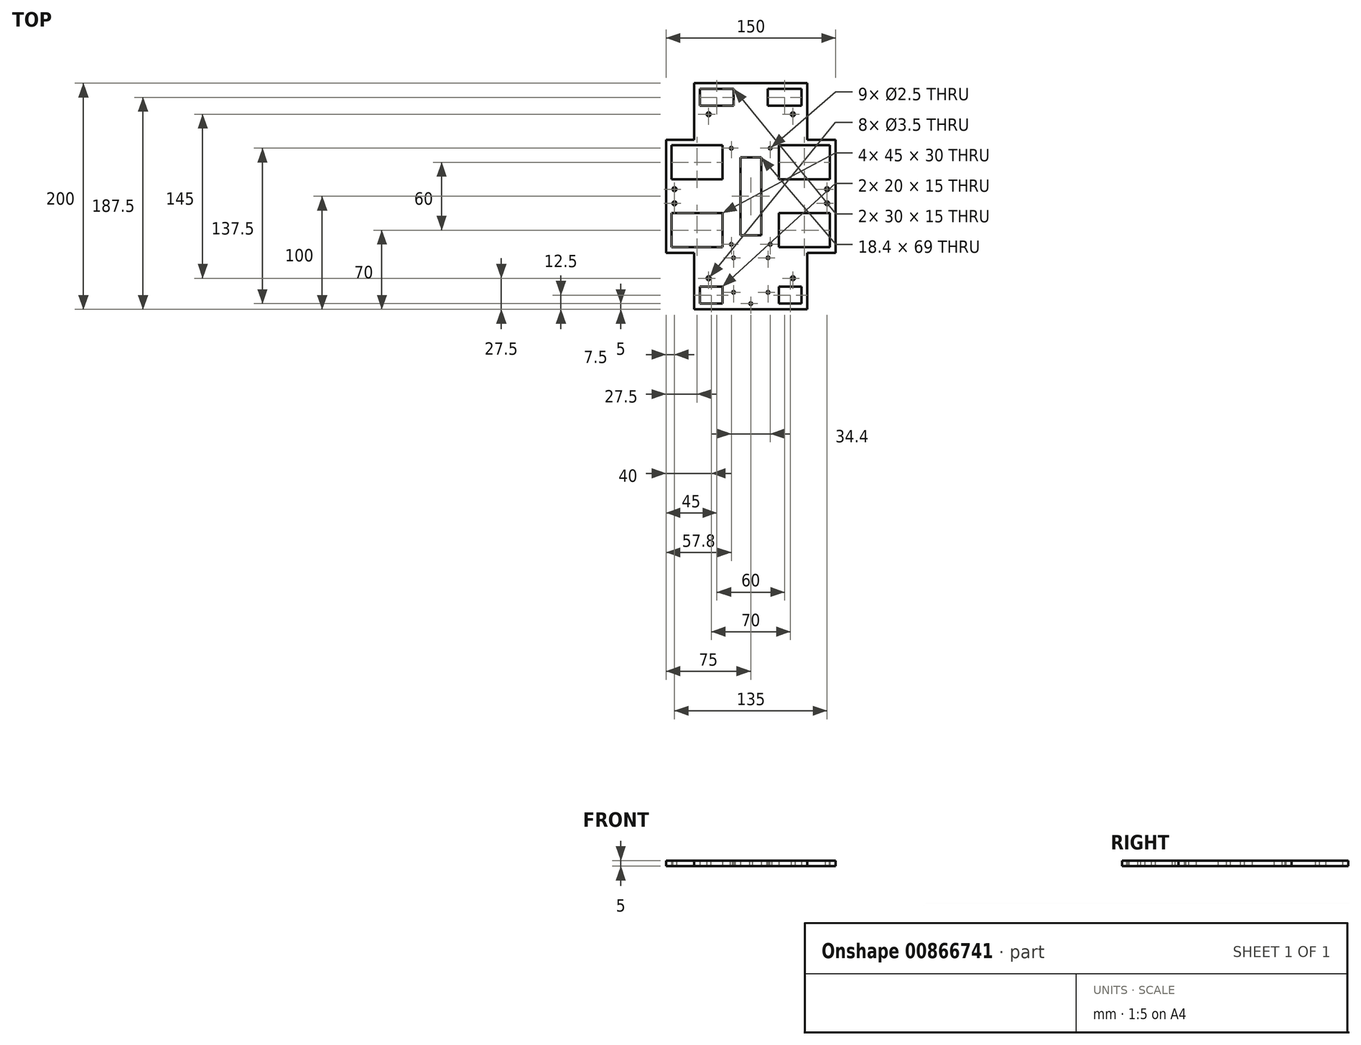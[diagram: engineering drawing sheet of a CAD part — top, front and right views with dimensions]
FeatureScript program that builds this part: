
annotation { "Feature Type Name" : "Feature", "Feature Type Description" : "" }
export const myFeature = defineFeature(function(context is Context, id is Id, definition is map)
    precondition{}
    {
        {
            assignVariable(context, id + "F0", {"variableType" : VariableType.LENGTH, "name" : "RackThickness", "lengthValue" : 5 * mm});
        }
        {
            var Q0;
            Q0=qCreatedBy(makeId("Top.planeOp"),FACE);
            var sketch = newSketch(context, id + "F1", { "sketchPlane" : qUnion([Q0])});
            skLineSegment(sketch, "E0.bottom", {"start": v(-50, 100) * mm, "end": v(50, 100) * mm});
            skLineSegment(sketch, "E0.top", {"start": v(-50, -100) * mm, "end": v(50, -100) * mm});
            skLineSegment(sketch, "E0.left", {"start": v(-50, 100) * mm, "end": v(-50, -100) * mm});
            skLineSegment(sketch, "E0.right", {"start": v(50, 100) * mm, "end": v(50, -100) * mm});
            skPoint(sketch, "E0.middle", {"position": v(0, 0) * mm});
            skLineSegment(sketch, "E1.bottom", {"start": v(75, -50) * mm, "end": v(-75, -50) * mm});
            skLineSegment(sketch, "E1.top", {"start": v(75, 50) * mm, "end": v(-75, 50) * mm});
            skLineSegment(sketch, "E1.left", {"start": v(75, -50) * mm, "end": v(75, 50) * mm});
            skLineSegment(sketch, "E1.right", {"start": v(-75, -50) * mm, "end": v(-75, 50) * mm});
            skLineSegment(sketch, "E2.bottom", {"start": v(37.25, -72.5) * mm, "end": v(-37.25, -72.5) * mm});
            skLineSegment(sketch, "E2.top", {"start": v(37.25, 72.5) * mm, "end": v(-37.25, 72.5) * mm});
            skLineSegment(sketch, "E2.left", {"start": v(37.25, -72.5) * mm, "end": v(37.25, 72.5) * mm});
            skLineSegment(sketch, "E2.right", {"start": v(-37.25, -72.5) * mm, "end": v(-37.25, 72.5) * mm});
            skLineSegment(sketch, "E3.bottom", {"start": v(67.5, -6.25) * mm, "end": v(-67.5, -6.25) * mm});
            skLineSegment(sketch, "E3.top", {"start": v(67.5, 6.25) * mm, "end": v(-67.5, 6.25) * mm});
            skLineSegment(sketch, "E3.left", {"start": v(67.5, -6.25) * mm, "end": v(67.5, 6.25) * mm});
            skLineSegment(sketch, "E3.right", {"start": v(-67.5, -6.25) * mm, "end": v(-67.5, 6.25) * mm});
            skCircle(sketch, "E4", {"center": v(-37.25, 72.5) * mm, "radius": 1.75 * mm});
            skCircle(sketch, "E5", {"center": v(37.25, 72.5) * mm, "radius": 1.75 * mm});
            skCircle(sketch, "E6", {"center": v(-67.5, 6.25) * mm, "radius": 1.75 * mm});
            skCircle(sketch, "E7", {"center": v(67.5, 6.25) * mm, "radius": 1.75 * mm});
            skCircle(sketch, "E8", {"center": v(67.5, -6.25) * mm, "radius": 1.75 * mm});
            skCircle(sketch, "E9", {"center": v(-67.5, -6.25) * mm, "radius": 1.75 * mm});
            skCircle(sketch, "E10", {"center": v(-37.25, -72.5) * mm, "radius": 1.75 * mm});
            skCircle(sketch, "E11", {"center": v(37.25, -72.5) * mm, "radius": 1.75 * mm});
            skPoint(sketch, "E12", {"position": v(-70, 50) * mm});
            skPoint(sketch, "E13", {"position": v(-75, 45) * mm});
            skPoint(sketch, "E14", {"position": v(-75, -45) * mm});
            skPoint(sketch, "E15", {"position": v(-70, -50) * mm});
            skPoint(sketch, "E16", {"position": v(-50, -95) * mm});
            skPoint(sketch, "E17", {"position": v(-45, -100) * mm});
            skPoint(sketch, "E18", {"position": v(-50, 95) * mm});
            skPoint(sketch, "E19", {"position": v(-45, 100) * mm});
            skPoint(sketch, "E20", {"position": v(45, -100) * mm});
            skPoint(sketch, "E21", {"position": v(50, -95) * mm});
            skPoint(sketch, "E22", {"position": v(70, -50) * mm});
            skPoint(sketch, "E23", {"position": v(75, -45) * mm});
            skPoint(sketch, "E24", {"position": v(75, 45) * mm});
            skPoint(sketch, "E25", {"position": v(70, 50) * mm});
            skPoint(sketch, "E26", {"position": v(50, 95) * mm});
            skPoint(sketch, "E27", {"position": v(45, 100) * mm});
            skLineSegment(sketch, "E28.bottom", {"start": v(-45, 95) * mm, "end": v(-15, 95) * mm});
            skLineSegment(sketch, "E28.top", {"start": v(-45, 80) * mm, "end": v(-15, 80) * mm});
            skLineSegment(sketch, "E28.left", {"start": v(-45, 95) * mm, "end": v(-45, 80) * mm});
            skLineSegment(sketch, "E28.right", {"start": v(-15, 95) * mm, "end": v(-15, 80) * mm});
            skLineSegment(sketch, "E29.bottom", {"start": v(45, 95) * mm, "end": v(15, 95) * mm});
            skLineSegment(sketch, "E29.top", {"start": v(45, 80) * mm, "end": v(15, 80) * mm});
            skLineSegment(sketch, "E29.left", {"start": v(45, 95) * mm, "end": v(45, 80) * mm});
            skLineSegment(sketch, "E29.right", {"start": v(15, 95) * mm, "end": v(15, 80) * mm});
            skLineSegment(sketch, "E30.bottom", {"start": v(70, 45) * mm, "end": v(25, 45) * mm});
            skLineSegment(sketch, "E30.top", {"start": v(70, 15) * mm, "end": v(25, 15) * mm});
            skLineSegment(sketch, "E30.left", {"start": v(70, 45) * mm, "end": v(70, 15) * mm});
            skLineSegment(sketch, "E30.right", {"start": v(25, 45) * mm, "end": v(25, 15) * mm});
            skLineSegment(sketch, "E31.bottom", {"start": v(70, -45) * mm, "end": v(25, -45) * mm});
            skLineSegment(sketch, "E31.top", {"start": v(70, -15) * mm, "end": v(25, -15) * mm});
            skLineSegment(sketch, "E31.left", {"start": v(70, -45) * mm, "end": v(70, -15) * mm});
            skLineSegment(sketch, "E31.right", {"start": v(25, -45) * mm, "end": v(25, -15) * mm});
            skLineSegment(sketch, "E32.bottom", {"start": v(-70, 45) * mm, "end": v(-25, 45) * mm});
            skLineSegment(sketch, "E32.top", {"start": v(-70, 15) * mm, "end": v(-25, 15) * mm});
            skLineSegment(sketch, "E32.left", {"start": v(-70, 45) * mm, "end": v(-70, 15) * mm});
            skLineSegment(sketch, "E32.right", {"start": v(-25, 45) * mm, "end": v(-25, 15) * mm});
            skLineSegment(sketch, "E33.bottom", {"start": v(-70, -45) * mm, "end": v(-25, -45) * mm});
            skLineSegment(sketch, "E33.top", {"start": v(-70, -15) * mm, "end": v(-25, -15) * mm});
            skLineSegment(sketch, "E33.left", {"start": v(-70, -45) * mm, "end": v(-70, -15) * mm});
            skLineSegment(sketch, "E33.right", {"start": v(-25, -45) * mm, "end": v(-25, -15) * mm});
            skLineSegment(sketch, "E34.bottom", {"start": v(-45, -95) * mm, "end": v(-25, -95) * mm});
            skLineSegment(sketch, "E34.top", {"start": v(-45, -80) * mm, "end": v(-25, -80) * mm});
            skLineSegment(sketch, "E34.left", {"start": v(-45, -95) * mm, "end": v(-45, -80) * mm});
            skLineSegment(sketch, "E34.right", {"start": v(-25, -95) * mm, "end": v(-25, -80) * mm});
            skLineSegment(sketch, "E35.bottom", {"start": v(45, -95) * mm, "end": v(25, -95) * mm});
            skLineSegment(sketch, "E35.top", {"start": v(45, -80) * mm, "end": v(25, -80) * mm});
            skLineSegment(sketch, "E35.left", {"start": v(45, -95) * mm, "end": v(45, -80) * mm});
            skLineSegment(sketch, "E35.right", {"start": v(25, -95) * mm, "end": v(25, -80) * mm});
            skSolve(sketch);
        }
        {
            var Q0;
            {var subQ0=sQuery(id+"F1.wireOp",EDGE,"E1.top");var subQ1=sQuery(id+"F1.wireOp",EDGE,"E0.left");var subQ2=makeQuery(id+"F1.imprint","INTERSECT",VERTEX,{"derivedFrom":[subQ1,subQ0]});Q0=makeQuery(id+"F1.imprint","IMPRINT",FACE,{"disambiguationData":[TD([[makeQuery(id+"F1.imprint","IMPRINT",EDGE,{"disambiguationData":[TD([[subQ2,-1.0]])],"derivedFrom":subQ1}),1.0]])]});}
            var sketch = newSketch(context, id + "F2", { "sketchPlane" : qUnion([Q0])});
            skLineSegment(sketch, "E36.bottom", {"start": v(17.2, -42.5) * mm, "end": v(-17.2, -42.5) * mm});
            skLineSegment(sketch, "E36.top", {"start": v(17.2, 42.5) * mm, "end": v(-17.2, 42.5) * mm});
            skLineSegment(sketch, "E36.left", {"start": v(17.2, -42.5) * mm, "end": v(17.2, 42.5) * mm});
            skLineSegment(sketch, "E36.right", {"start": v(-17.2, -42.5) * mm, "end": v(-17.2, 42.5) * mm});
            skPoint(sketch, "E36.middle", {"position": v(0, 0) * mm});
            skCircle(sketch, "E37", {"center": v(-17.2, 42.5) * mm, "radius": 1.25 * mm});
            skCircle(sketch, "E38", {"center": v(17.2, 42.5) * mm, "radius": 1.25 * mm});
            skCircle(sketch, "E39", {"center": v(-17.2, -42.5) * mm, "radius": 1.25 * mm});
            skCircle(sketch, "E40", {"center": v(17.2, -42.5) * mm, "radius": 1.25 * mm});
            skPoint(sketch, "E41", {"position": v(0, -100) * mm});
            skLineSegment(sketch, "E42", {"start": v(0, -100) * mm, "end": v(0, -69.75) * mm});
            skLineSegment(sketch, "E43.bottom", {"start": v(15.25, -54.5) * mm, "end": v(-15.25, -54.5) * mm});
            skLineSegment(sketch, "E43.top", {"start": v(15.25, -85) * mm, "end": v(-15.25, -85) * mm});
            skLineSegment(sketch, "E43.left", {"start": v(15.25, -54.5) * mm, "end": v(15.25, -85) * mm});
            skLineSegment(sketch, "E43.right", {"start": v(-15.25, -54.5) * mm, "end": v(-15.25, -85) * mm});
            skPoint(sketch, "E43.middle", {"position": v(0, -69.75) * mm});
            skCircle(sketch, "E44", {"center": v(-15.25, -54.5) * mm, "radius": 1.25 * mm});
            skCircle(sketch, "E45", {"center": v(15.25, -54.5) * mm, "radius": 1.25 * mm});
            skCircle(sketch, "E46", {"center": v(15.25, -85) * mm, "radius": 1.25 * mm});
            skCircle(sketch, "E47", {"center": v(-15.25, -85) * mm, "radius": 1.25 * mm});
            skLineSegment(sketch, "E48.bottom", {"start": v(9.2, 34.5) * mm, "end": v(-9.2, 34.5) * mm});
            skLineSegment(sketch, "E48.top", {"start": v(9.2, -34.5) * mm, "end": v(-9.2, -34.5) * mm});
            skLineSegment(sketch, "E48.left", {"start": v(9.2, 34.5) * mm, "end": v(9.2, -34.5) * mm});
            skLineSegment(sketch, "E48.right", {"start": v(-9.2, 34.5) * mm, "end": v(-9.2, -34.5) * mm});
            skPoint(sketch, "E49", {"position": v(0, -95) * mm});
            skPoint(sketch, "E50", {"position": v(0, -85) * mm});
            skCircle(sketch, "E51", {"center": v(0, -85) * mm, "radius": 1.25 * mm});
            skCircle(sketch, "E52", {"center": v(0, -95) * mm, "radius": 1.25 * mm});
            skSolve(sketch);
        }
        {
            var Q0;
            Q0 = qSketchRegion(id + "F1", true);
            var Q1;
            {var subQ1=sQuery(id+"F1.wireOp",EDGE,"E1.bottom");var subQ5=sQuery(id+"F1.wireOp",EDGE,"E2.left");var subQ6=makeQuery(id+"F1.imprint","INTERSECT",VERTEX,{"derivedFrom":[subQ1,subQ5]});Q1=makeQuery(id+"F1.imprint","IMPRINT",FACE,{"disambiguationData":[TD([[makeQuery(id+"F1.imprint","IMPRINT",EDGE,{"disambiguationData":[TD([[subQ6,-1.0]])],"derivedFrom":subQ1}),1.0]])]});}
            var Q2;
            {var subQ0=sQuery(id+"F1.wireOp",EDGE,"E31.right");Q2=makeQuery(id+"F1.imprint","IMPRINT",FACE,{"disambiguationData":[TD([[makeQuery(id+"F1.imprint","IMPRINT",EDGE,{"derivedFrom":subQ0}),1.0]])]});}
            var Q3;
            {var subQ4=sQuery(id+"F1.wireOp",EDGE,"E30.right");Q3=makeQuery(id+"F1.imprint","IMPRINT",FACE,{"disambiguationData":[TD([[makeQuery(id+"F1.imprint","IMPRINT",EDGE,{"derivedFrom":subQ4}),-1.0]])]});}
            var Q4;
            {var subQ1=sQuery(id+"F1.wireOp",EDGE,"E1.top");var subQ9=sQuery(id+"F1.wireOp",EDGE,"E2.left");var subQ10=makeQuery(id+"F1.imprint","INTERSECT",VERTEX,{"derivedFrom":[subQ1,subQ9]});Q4=makeQuery(id+"F1.imprint","IMPRINT",FACE,{"disambiguationData":[TD([[makeQuery(id+"F1.imprint","IMPRINT",EDGE,{"disambiguationData":[TD([[subQ10,-1.0]])],"derivedFrom":subQ1}),-1.0]])]});}
            var Q5;
            {var subQ0=sQuery(id+"F1.wireOp",EDGE,"E3.bottom");var subQ1=sQuery(id+"F1.wireOp",EDGE,"E2.left");var subQ2=makeQuery(id+"F1.imprint","INTERSECT",VERTEX,{"derivedFrom":[subQ1,subQ0]});Q5=makeQuery(id+"F1.imprint","IMPRINT",FACE,{"disambiguationData":[TD([[makeQuery(id+"F1.imprint","IMPRINT",EDGE,{"disambiguationData":[TD([[subQ2,-1.0]])],"derivedFrom":subQ1}),1.0]])]});}
            var Q6;
            {var subQ0=sQuery(id+"F1.wireOp",EDGE,"E32.top");var subQ1=sQuery(id+"F1.wireOp",EDGE,"E0.left");var subQ2=makeQuery(id+"F1.imprint","INTERSECT",VERTEX,{"derivedFrom":[subQ1,subQ0]});Q6=makeQuery(id+"F1.imprint","IMPRINT",FACE,{"disambiguationData":[TD([[makeQuery(id+"F1.imprint","IMPRINT",EDGE,{"disambiguationData":[TD([[subQ2,-1.0]])],"derivedFrom":subQ1}),1.0]])]});}
            var Q7;
            {var subQ0=sQuery(id+"F1.wireOp",EDGE,"E3.bottom");var subQ1=sQuery(id+"F1.wireOp",EDGE,"E0.left");var subQ2=makeQuery(id+"F1.imprint","INTERSECT",VERTEX,{"derivedFrom":[subQ1,subQ0]});Q7=makeQuery(id+"F1.imprint","IMPRINT",FACE,{"disambiguationData":[TD([[makeQuery(id+"F1.imprint","IMPRINT",EDGE,{"disambiguationData":[TD([[subQ2,-1.0]])],"derivedFrom":subQ1}),1.0]])]});}
            var Q8;
            {var subQ0=sQuery(id+"F1.wireOp",EDGE,"E3.top");var subQ1=sQuery(id+"F1.wireOp",EDGE,"E0.left");var subQ2=makeQuery(id+"F1.imprint","INTERSECT",VERTEX,{"derivedFrom":[subQ1,subQ0]});Q8=makeQuery(id+"F1.imprint","IMPRINT",FACE,{"disambiguationData":[TD([[makeQuery(id+"F1.imprint","IMPRINT",EDGE,{"disambiguationData":[TD([[subQ2,-1.0]])],"derivedFrom":subQ1}),1.0]])]});}
            var Q9;
            {var subQ0=sQuery(id+"F1.wireOp",EDGE,"E3.bottom");var subQ1=sQuery(id+"F1.wireOp",EDGE,"E0.right");var subQ2=makeQuery(id+"F1.imprint","INTERSECT",VERTEX,{"derivedFrom":[subQ1,subQ0]});Q9=makeQuery(id+"F1.imprint","IMPRINT",FACE,{"disambiguationData":[TD([[makeQuery(id+"F1.imprint","IMPRINT",EDGE,{"disambiguationData":[TD([[subQ2,-1.0]])],"derivedFrom":subQ1}),-1.0]])]});}
            var Q10;
            {var subQ0=sQuery(id+"F1.wireOp",EDGE,"E3.top");var subQ1=sQuery(id+"F1.wireOp",EDGE,"E0.right");var subQ2=makeQuery(id+"F1.imprint","INTERSECT",VERTEX,{"derivedFrom":[subQ1,subQ0]});Q10=makeQuery(id+"F1.imprint","IMPRINT",FACE,{"disambiguationData":[TD([[makeQuery(id+"F1.imprint","IMPRINT",EDGE,{"disambiguationData":[TD([[subQ2,-1.0]])],"derivedFrom":subQ1}),-1.0]])]});}
            var Q11;
            {var subQ0=sQuery(id+"F1.wireOp",EDGE,"E30.top");var subQ1=sQuery(id+"F1.wireOp",EDGE,"E0.right");var subQ2=makeQuery(id+"F1.imprint","INTERSECT",VERTEX,{"derivedFrom":[subQ1,subQ0]});Q11=makeQuery(id+"F1.imprint","IMPRINT",FACE,{"disambiguationData":[TD([[makeQuery(id+"F1.imprint","IMPRINT",EDGE,{"disambiguationData":[TD([[subQ2,-1.0]])],"derivedFrom":subQ1}),-1.0]])]});}
            var Q12;
            {var subQ0=sQuery(id+"F1.wireOp",EDGE,"E3.top");var subQ1=sQuery(id+"F1.wireOp",EDGE,"E0.right");var subQ2=makeQuery(id+"F1.imprint","INTERSECT",VERTEX,{"derivedFrom":[subQ1,subQ0]});Q12=makeQuery(id+"F1.imprint","IMPRINT",FACE,{"disambiguationData":[TD([[makeQuery(id+"F1.imprint","IMPRINT",EDGE,{"disambiguationData":[TD([[subQ2,-1.0]])],"derivedFrom":subQ1}),1.0]])]});}
            var Q13;
            {var subQ5=sQuery(id+"F1.wireOp",EDGE,"E3.top");var subQ6=sQuery(id+"F1.wireOp",EDGE,"E0.left");var subQ7=makeQuery(id+"F1.imprint","INTERSECT",VERTEX,{"derivedFrom":[subQ6,subQ5]});Q13=makeQuery(id+"F1.imprint","IMPRINT",FACE,{"disambiguationData":[TD([[makeQuery(id+"F1.imprint","IMPRINT",EDGE,{"disambiguationData":[TD([[subQ7,-1.0]])],"derivedFrom":subQ6}),-1.0]])]});}
            extrude(context, id + "F3", {"entities" : qUnion([Q0, Q1, Q2, Q3, Q4, Q5, Q6, Q7, Q8, Q9, Q10, Q11, Q12, Q13]), "depth" : getVariable(context, 'RackThickness'), "offsetDistance" : 25 * mm});
        }
        {
            var Q0;
            {var subQ0=sQuery(id+"F2.wireOp",EDGE,"E43.left");var subQ1=sQuery(id+"F2.wireOp",EDGE,"E43.top");var subQ2=makeQuery(id+"F2.imprint","INTERSECT",VERTEX,{"derivedFrom":[subQ1,subQ0]});Q0=makeQuery(id+"F2.imprint","IMPRINT",FACE,{"disambiguationData":[TD([[makeQuery(id+"F2.imprint","IMPRINT",EDGE,{"disambiguationData":[TD([[subQ2,-1.0]])],"derivedFrom":subQ1}),1.0]])]});}
            var Q1;
            {var subQ0=sQuery(id+"F2.wireOp",EDGE,"E51");var subQ1=sQuery(id+"F2.wireOp",EDGE,"E42");var subQ2=makeQuery(id+"F2.imprint","INTERSECT",VERTEX,{"disambiguationData":[OD(0.0)],"derivedFrom":[subQ1,subQ0]});Q1=makeQuery(id+"F2.imprint","IMPRINT",FACE,{"disambiguationData":[TD([[makeQuery(id+"F2.imprint","IMPRINT",EDGE,{"disambiguationData":[TD([[subQ2,-1.0]])],"derivedFrom":subQ1}),1.0]])]});}
            var Q2;
            {var subQ0=sQuery(id+"F2.wireOp",EDGE,"E51");var subQ1=sQuery(id+"F2.wireOp",EDGE,"E42");var subQ2=makeQuery(id+"F2.imprint","INTERSECT",VERTEX,{"disambiguationData":[OD(1.0)],"derivedFrom":[subQ1,subQ0]});Q2=makeQuery(id+"F2.imprint","IMPRINT",FACE,{"disambiguationData":[TD([[makeQuery(id+"F2.imprint","IMPRINT",EDGE,{"disambiguationData":[TD([[subQ2,1.0]])],"derivedFrom":subQ1}),-1.0]])]});}
            var Q3;
            {var subQ0=sQuery(id+"F2.wireOp",EDGE,"E51");var subQ1=sQuery(id+"F2.wireOp",EDGE,"E42");var subQ2=makeQuery(id+"F2.imprint","INTERSECT",VERTEX,{"disambiguationData":[OD(0.0)],"derivedFrom":[subQ1,subQ0]});Q3=makeQuery(id+"F2.imprint","IMPRINT",FACE,{"disambiguationData":[TD([[makeQuery(id+"F2.imprint","IMPRINT",EDGE,{"disambiguationData":[TD([[subQ2,-1.0]])],"derivedFrom":subQ1}),-1.0]])]});}
            var Q4;
            {var subQ0=sQuery(id+"F2.wireOp",EDGE,"E51");var subQ1=sQuery(id+"F2.wireOp",EDGE,"E42");var subQ2=makeQuery(id+"F2.imprint","INTERSECT",VERTEX,{"disambiguationData":[OD(1.0)],"derivedFrom":[subQ1,subQ0]});Q4=makeQuery(id+"F2.imprint","IMPRINT",FACE,{"disambiguationData":[TD([[makeQuery(id+"F2.imprint","IMPRINT",EDGE,{"disambiguationData":[TD([[subQ2,1.0]])],"derivedFrom":subQ1}),1.0]])]});}
            var Q5;
            {var subQ0=sQuery(id+"F2.wireOp",EDGE,"E52");var subQ1=sQuery(id+"F2.wireOp",EDGE,"E42");var subQ2=makeQuery(id+"F2.imprint","INTERSECT",VERTEX,{"disambiguationData":[OD(0.0)],"derivedFrom":[subQ1,subQ0]});Q5=makeQuery(id+"F2.imprint","IMPRINT",FACE,{"disambiguationData":[TD([[makeQuery(id+"F2.imprint","IMPRINT",EDGE,{"disambiguationData":[TD([[subQ2,-1.0]])],"derivedFrom":subQ1}),1.0]])]});}
            var Q6;
            {var subQ0=sQuery(id+"F2.wireOp",EDGE,"E52");var subQ1=sQuery(id+"F2.wireOp",EDGE,"E42");var subQ2=makeQuery(id+"F2.imprint","INTERSECT",VERTEX,{"disambiguationData":[OD(0.0)],"derivedFrom":[subQ1,subQ0]});Q6=makeQuery(id+"F2.imprint","IMPRINT",FACE,{"disambiguationData":[TD([[makeQuery(id+"F2.imprint","IMPRINT",EDGE,{"disambiguationData":[TD([[subQ2,-1.0]])],"derivedFrom":subQ1}),-1.0]])]});}
            var Q7;
            {var subQ0=sQuery(id+"F2.wireOp",EDGE,"E43.left");var subQ1=sQuery(id+"F2.wireOp",EDGE,"E43.top");var subQ2=makeQuery(id+"F2.imprint","INTERSECT",VERTEX,{"derivedFrom":[subQ1,subQ0]});Q7=makeQuery(id+"F2.imprint","IMPRINT",FACE,{"disambiguationData":[TD([[makeQuery(id+"F2.imprint","IMPRINT",EDGE,{"disambiguationData":[TD([[subQ2,-1.0]])],"derivedFrom":subQ1}),-1.0]])]});}
            var Q8;
            {var subQ0=sQuery(id+"F2.wireOp",EDGE,"E43.right");var subQ1=sQuery(id+"F2.wireOp",EDGE,"E43.top");var subQ2=makeQuery(id+"F2.imprint","INTERSECT",VERTEX,{"derivedFrom":[subQ1,subQ0]});Q8=makeQuery(id+"F2.imprint","IMPRINT",FACE,{"disambiguationData":[TD([[makeQuery(id+"F2.imprint","IMPRINT",EDGE,{"disambiguationData":[TD([[subQ2,1.0]])],"derivedFrom":subQ1}),1.0]])]});}
            var Q9;
            {var subQ0=sQuery(id+"F2.wireOp",EDGE,"E43.right");var subQ1=sQuery(id+"F2.wireOp",EDGE,"E43.top");var subQ2=makeQuery(id+"F2.imprint","INTERSECT",VERTEX,{"derivedFrom":[subQ1,subQ0]});Q9=makeQuery(id+"F2.imprint","IMPRINT",FACE,{"disambiguationData":[TD([[makeQuery(id+"F2.imprint","IMPRINT",EDGE,{"disambiguationData":[TD([[subQ2,1.0]])],"derivedFrom":subQ1}),-1.0]])]});}
            var Q10;
            {var subQ0=sQuery(id+"F2.wireOp",EDGE,"E43.left");var subQ1=sQuery(id+"F2.wireOp",EDGE,"E43.bottom");var subQ2=makeQuery(id+"F2.imprint","INTERSECT",VERTEX,{"derivedFrom":[subQ1,subQ0]});Q10=makeQuery(id+"F2.imprint","IMPRINT",FACE,{"disambiguationData":[TD([[makeQuery(id+"F2.imprint","IMPRINT",EDGE,{"disambiguationData":[TD([[subQ2,-1.0]])],"derivedFrom":subQ1}),-1.0]])]});}
            var Q11;
            {var subQ0=sQuery(id+"F2.wireOp",EDGE,"E43.left");var subQ1=sQuery(id+"F2.wireOp",EDGE,"E43.bottom");var subQ2=makeQuery(id+"F2.imprint","INTERSECT",VERTEX,{"derivedFrom":[subQ1,subQ0]});Q11=makeQuery(id+"F2.imprint","IMPRINT",FACE,{"disambiguationData":[TD([[makeQuery(id+"F2.imprint","IMPRINT",EDGE,{"disambiguationData":[TD([[subQ2,-1.0]])],"derivedFrom":subQ1}),1.0]])]});}
            var Q12;
            {var subQ0=sQuery(id+"F2.wireOp",EDGE,"E43.right");var subQ1=sQuery(id+"F2.wireOp",EDGE,"E43.bottom");var subQ2=makeQuery(id+"F2.imprint","INTERSECT",VERTEX,{"derivedFrom":[subQ1,subQ0]});Q12=makeQuery(id+"F2.imprint","IMPRINT",FACE,{"disambiguationData":[TD([[makeQuery(id+"F2.imprint","IMPRINT",EDGE,{"disambiguationData":[TD([[subQ2,1.0]])],"derivedFrom":subQ1}),1.0]])]});}
            var Q13;
            {var subQ0=sQuery(id+"F2.wireOp",EDGE,"E43.right");var subQ1=sQuery(id+"F2.wireOp",EDGE,"E43.bottom");var subQ2=makeQuery(id+"F2.imprint","INTERSECT",VERTEX,{"derivedFrom":[subQ1,subQ0]});Q13=makeQuery(id+"F2.imprint","IMPRINT",FACE,{"disambiguationData":[TD([[makeQuery(id+"F2.imprint","IMPRINT",EDGE,{"disambiguationData":[TD([[subQ2,1.0]])],"derivedFrom":subQ1}),-1.0]])]});}
            var Q14;
            {var subQ0=sQuery(id+"F2.wireOp",EDGE,"E36.left");var subQ1=sQuery(id+"F2.wireOp",EDGE,"E36.bottom");var subQ2=makeQuery(id+"F2.imprint","INTERSECT",VERTEX,{"derivedFrom":[subQ1,subQ0]});Q14=makeQuery(id+"F2.imprint","IMPRINT",FACE,{"disambiguationData":[TD([[makeQuery(id+"F2.imprint","IMPRINT",EDGE,{"disambiguationData":[TD([[subQ2,-1.0]])],"derivedFrom":subQ1}),1.0]])]});}
            var Q15;
            {var subQ0=sQuery(id+"F2.wireOp",EDGE,"E36.left");var subQ1=sQuery(id+"F2.wireOp",EDGE,"E36.bottom");var subQ2=makeQuery(id+"F2.imprint","INTERSECT",VERTEX,{"derivedFrom":[subQ1,subQ0]});Q15=makeQuery(id+"F2.imprint","IMPRINT",FACE,{"disambiguationData":[TD([[makeQuery(id+"F2.imprint","IMPRINT",EDGE,{"disambiguationData":[TD([[subQ2,-1.0]])],"derivedFrom":subQ1}),-1.0]])]});}
            var Q16;
            {var subQ0=sQuery(id+"F2.wireOp",EDGE,"E36.right");var subQ1=sQuery(id+"F2.wireOp",EDGE,"E36.bottom");var subQ2=makeQuery(id+"F2.imprint","INTERSECT",VERTEX,{"derivedFrom":[subQ1,subQ0]});Q16=makeQuery(id+"F2.imprint","IMPRINT",FACE,{"disambiguationData":[TD([[makeQuery(id+"F2.imprint","IMPRINT",EDGE,{"disambiguationData":[TD([[subQ2,1.0]])],"derivedFrom":subQ1}),-1.0]])]});}
            var Q17;
            {var subQ0=sQuery(id+"F2.wireOp",EDGE,"E36.right");var subQ1=sQuery(id+"F2.wireOp",EDGE,"E36.bottom");var subQ2=makeQuery(id+"F2.imprint","INTERSECT",VERTEX,{"derivedFrom":[subQ1,subQ0]});Q17=makeQuery(id+"F2.imprint","IMPRINT",FACE,{"disambiguationData":[TD([[makeQuery(id+"F2.imprint","IMPRINT",EDGE,{"disambiguationData":[TD([[subQ2,1.0]])],"derivedFrom":subQ1}),1.0]])]});}
            var Q18;
            {var subQ0=sQuery(id+"F2.wireOp",EDGE,"E36.right");var subQ1=sQuery(id+"F2.wireOp",EDGE,"E36.top");var subQ2=makeQuery(id+"F2.imprint","INTERSECT",VERTEX,{"derivedFrom":[subQ1,subQ0]});Q18=makeQuery(id+"F2.imprint","IMPRINT",FACE,{"disambiguationData":[TD([[makeQuery(id+"F2.imprint","IMPRINT",EDGE,{"disambiguationData":[TD([[subQ2,1.0]])],"derivedFrom":subQ1}),-1.0]])]});}
            var Q19;
            {var subQ0=sQuery(id+"F2.wireOp",EDGE,"E36.right");var subQ1=sQuery(id+"F2.wireOp",EDGE,"E36.top");var subQ2=makeQuery(id+"F2.imprint","INTERSECT",VERTEX,{"derivedFrom":[subQ1,subQ0]});Q19=makeQuery(id+"F2.imprint","IMPRINT",FACE,{"disambiguationData":[TD([[makeQuery(id+"F2.imprint","IMPRINT",EDGE,{"disambiguationData":[TD([[subQ2,1.0]])],"derivedFrom":subQ1}),1.0]])]});}
            var Q20;
            {var subQ0=sQuery(id+"F2.wireOp",EDGE,"E36.left");var subQ1=sQuery(id+"F2.wireOp",EDGE,"E36.top");var subQ2=makeQuery(id+"F2.imprint","INTERSECT",VERTEX,{"derivedFrom":[subQ1,subQ0]});Q20=makeQuery(id+"F2.imprint","IMPRINT",FACE,{"disambiguationData":[TD([[makeQuery(id+"F2.imprint","IMPRINT",EDGE,{"disambiguationData":[TD([[subQ2,-1.0]])],"derivedFrom":subQ1}),1.0]])]});}
            var Q21;
            {var subQ0=sQuery(id+"F2.wireOp",EDGE,"E36.left");var subQ1=sQuery(id+"F2.wireOp",EDGE,"E36.top");var subQ2=makeQuery(id+"F2.imprint","INTERSECT",VERTEX,{"derivedFrom":[subQ1,subQ0]});Q21=makeQuery(id+"F2.imprint","IMPRINT",FACE,{"disambiguationData":[TD([[makeQuery(id+"F2.imprint","IMPRINT",EDGE,{"disambiguationData":[TD([[subQ2,-1.0]])],"derivedFrom":subQ1}),-1.0]])]});}
            var Q22;
            Q22=makeQuery(id+"F2.imprint","IMPRINT",FACE,{"disambiguationData":[TD([[makeQuery(id+"F2.imprint","IMPRINT",EDGE,{"derivedFrom":sQuery(id+"F2.wireOp",EDGE,"E48.bottom")}),1.0]])]});
            extrude(context, id + "F4", {"entities" : qUnion([Q0, Q1, Q2, Q3, Q4, Q5, Q6, Q7, Q8, Q9, Q10, Q11, Q12, Q13, Q14, Q15, Q16, Q17, Q18, Q19, Q20, Q21, Q22]), "operationType" : NewBodyOperationType.REMOVE, "depth" : getVariable(context, 'RackThickness'), "offsetDistance" : 25 * mm});
        }
    });
